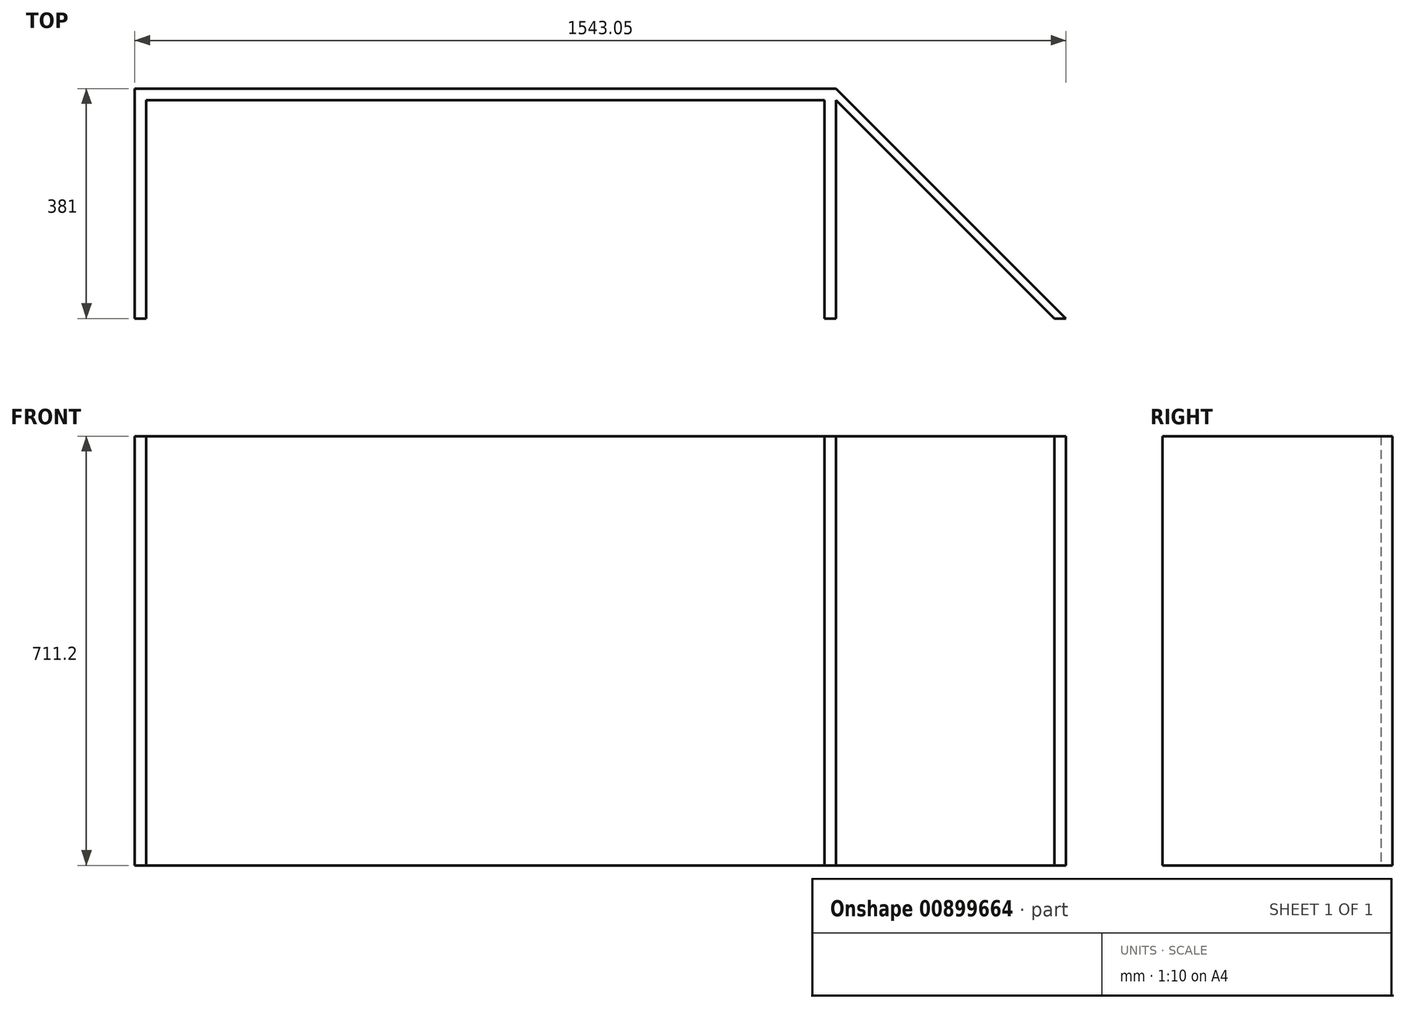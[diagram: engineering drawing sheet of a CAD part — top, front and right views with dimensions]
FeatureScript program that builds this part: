
annotation { "Feature Type Name" : "Feature", "Feature Type Description" : "" }
export const myFeature = defineFeature(function(context is Context, id is Id, definition is map)
    precondition{}
    {
        {
            var Q0;
            Q0=qCreatedBy(makeId("Top.planeOp"),FACE);
            var sketch = newSketch(context, id + "F0", { "sketchPlane" : qUnion([Q0])});
            skLineSegment(sketch, "E0.bottom", {"start": v(-19.05, 381) * mm, "end": v(0, 381) * mm});
            skLineSegment(sketch, "E0.top", {"start": v(-19.05, 0) * mm, "end": v(0, 0) * mm});
            skLineSegment(sketch, "E0.left", {"start": v(-19.05, 381) * mm, "end": v(-19.05, 0) * mm});
            skLineSegment(sketch, "E0.right", {"start": v(0, 381) * mm, "end": v(0, 0) * mm});
            skLineSegment(sketch, "E1.left", {"start": v(0, 0) * mm, "end": v(7.6, 17.47) * mm});
            skLineSegment(sketch, "E2.bottom", {"start": v(0, 381) * mm, "end": v(1143, 381) * mm});
            skLineSegment(sketch, "E2.top", {"start": v(0, 361.95) * mm, "end": v(1143, 361.95) * mm});
            skLineSegment(sketch, "E2.left", {"start": v(0, 381) * mm, "end": v(0, 361.95) * mm});
            skLineSegment(sketch, "E2.right", {"start": v(1143, 381) * mm, "end": v(1143, 361.95) * mm});
            skLineSegment(sketch, "E3.bottom", {"start": v(1143, 361.95) * mm, "end": v(1123.95, 361.95) * mm});
            skLineSegment(sketch, "E3.top", {"start": v(1143, 0) * mm, "end": v(1123.95, 0) * mm});
            skLineSegment(sketch, "E3.left", {"start": v(1143, 361.95) * mm, "end": v(1143, 0) * mm});
            skLineSegment(sketch, "E3.right", {"start": v(1123.95, 361.95) * mm, "end": v(1123.95, 0) * mm});
            skLineSegment(sketch, "E4", {"start": v(0, 0) * mm, "end": v(1575.62, 0) * mm, "construction": true});
            skLineSegment(sketch, "E5", {"start": v(1143, 361.95) * mm, "end": v(1504.95, 0) * mm});
            skLineSegment(sketch, "E6", {"start": v(1504.95, 0) * mm, "end": v(1524, 0) * mm});
            skLineSegment(sketch, "E7", {"start": v(1524, 0) * mm, "end": v(1143, 381) * mm});
            skSolve(sketch);
        }
        {
            var Q0;
            {var subQ3=sQuery(id+"F0.wireOp",EDGE,"E0.bottom");Q0=makeQuery(id+"F0.imprint","IMPRINT",FACE,{"disambiguationData":[TD([[makeQuery(id+"F0.imprint","IMPRINT",EDGE,{"derivedFrom":subQ3}),-1.0]])]});}
            var Q1;
            {var subQ5=sQuery(id+"F0.wireOp",EDGE,"E2.bottom");Q1=makeQuery(id+"F0.imprint","IMPRINT",FACE,{"disambiguationData":[TD([[makeQuery(id+"F0.imprint","IMPRINT",EDGE,{"derivedFrom":subQ5}),-1.0]])]});}
            var Q2;
            Q2=makeQuery(id+"F0.imprint","IMPRINT",FACE,{"disambiguationData":[TD([[makeQuery(id+"F0.imprint","IMPRINT",EDGE,{"derivedFrom":sQuery(id+"F0.wireOp",EDGE,"E3.top")}),-1.0]])]});
            var Q3;
            Q3=makeQuery(id+"F0.imprint","IMPRINT",FACE,{"disambiguationData":[TD([[makeQuery(id+"F0.imprint","IMPRINT",EDGE,{"derivedFrom":sQuery(id+"F0.wireOp",EDGE,"E2.right")}),1.0]])]});
            extrude(context, id + "F1", {"entities" : qUnion([Q0, Q1, Q2, Q3]), "depth" : 711.2 * mm, "offsetDistance" : 25.4 * mm});
        }
    });
